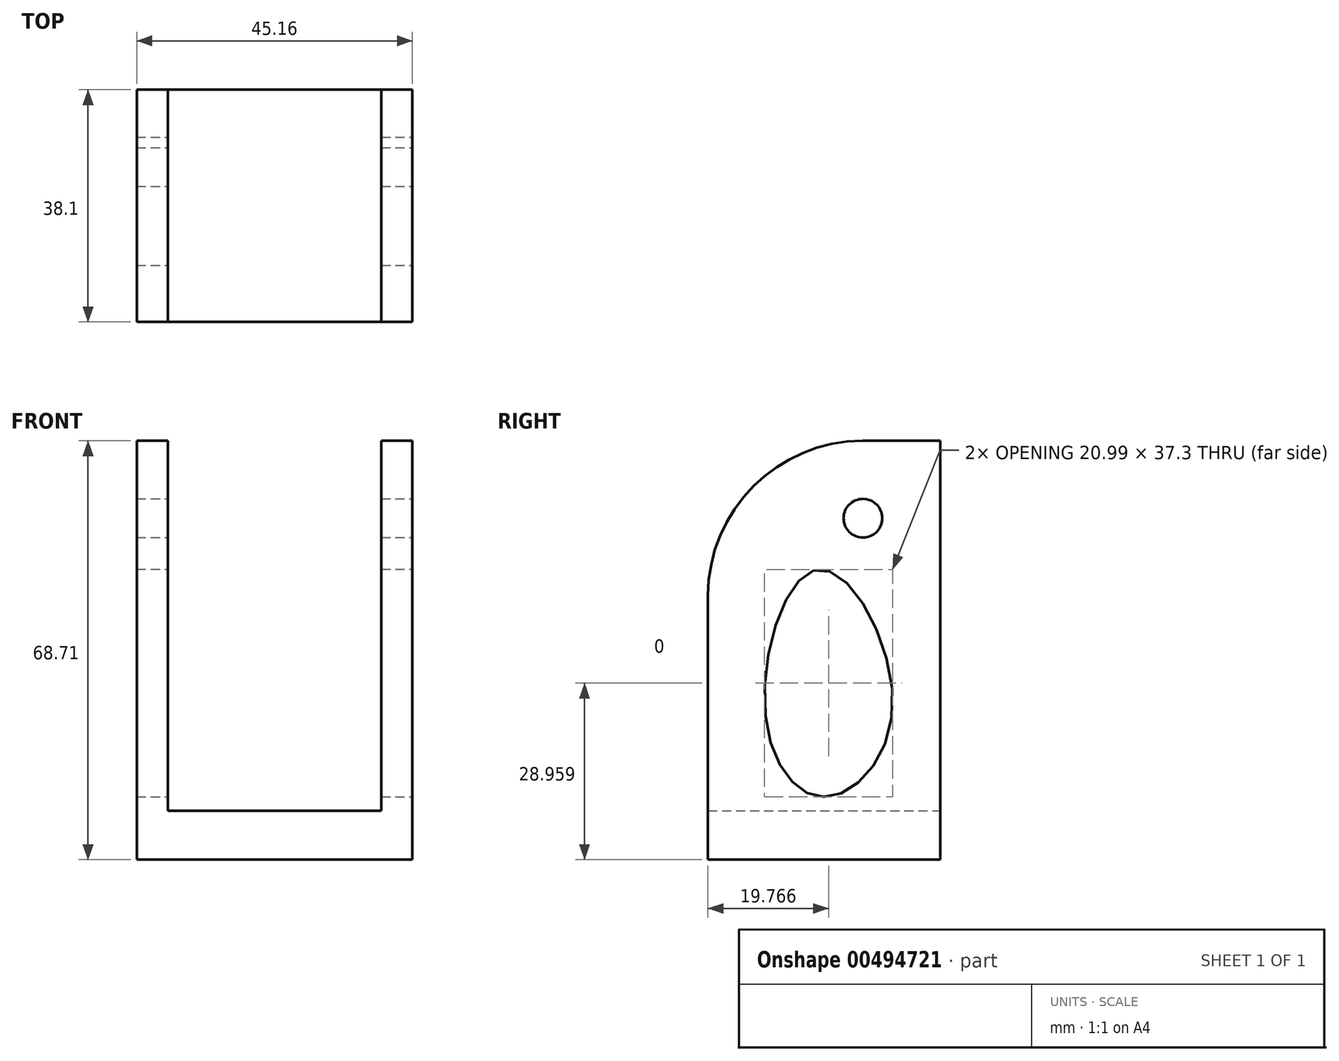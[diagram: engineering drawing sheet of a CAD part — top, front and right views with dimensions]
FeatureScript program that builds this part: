
annotation { "Feature Type Name" : "Feature", "Feature Type Description" : "" }
export const myFeature = defineFeature(function(context is Context, id is Id, definition is map)
    precondition{}
    {
        {
            var Q0;
            Q0=qCreatedBy(makeId("Front.planeOp"),FACE);
            var sketch = newSketch(context, id + "F0", { "sketchPlane" : qUnion([Q0])});
            skLineSegment(sketch, "E0.bottom", {"start": v(0, 0) * mm, "end": v(-45.16, 0) * mm});
            skLineSegment(sketch, "E0.top", {"start": v(0, 8.02) * mm, "end": v(-45.16, 8.02) * mm});
            skLineSegment(sketch, "E0.left", {"start": v(0, 0) * mm, "end": v(0, 8.02) * mm});
            skLineSegment(sketch, "E0.right", {"start": v(-45.16, 0) * mm, "end": v(-45.16, 8.02) * mm});
            skLineSegment(sketch, "E1.bottom", {"start": v(-45.16, 8.02) * mm, "end": v(-40.08, 8.02) * mm});
            skLineSegment(sketch, "E1.top", {"start": v(-45.16, 68.71) * mm, "end": v(-40.08, 68.71) * mm});
            skLineSegment(sketch, "E1.left", {"start": v(-45.16, 8.02) * mm, "end": v(-45.16, 68.71) * mm});
            skLineSegment(sketch, "E1.right", {"start": v(-40.08, 8.02) * mm, "end": v(-40.08, 68.71) * mm});
            skLineSegment(sketch, "E2.bottom", {"start": v(0, 8.02) * mm, "end": v(-5.08, 8.02) * mm});
            skLineSegment(sketch, "E2.top", {"start": v(0, 68.71) * mm, "end": v(-5.08, 68.71) * mm});
            skLineSegment(sketch, "E2.left", {"start": v(0, 8.02) * mm, "end": v(0, 68.71) * mm});
            skLineSegment(sketch, "E2.right", {"start": v(-5.08, 8.02) * mm, "end": v(-5.08, 68.71) * mm});
            skSolve(sketch);
        }
        {
            var Q0;
            Q0=qSketchRegion(id+"F0",true);
            var Q1;
            Q1=qSketchRegion(id+"F2",true);
            extrude(context, id + "F1", {"entities" : qUnion([Q0, Q1]), "depth" : 38.1 * mm});
        }
        {
            var Q0;
            Q0=qCreatedBy(makeId("Right.planeOp"),FACE);
            var sketch = newSketch(context, id + "F2", { "sketchPlane" : qUnion([Q0])});
            skPoint(sketch, "E3", {"position": v(-12.7, 56.01) * mm});
            skFitSpline(sketch, "E4", {"points": [v(-19.14, 10.3) * mm, v(-28.72, 24.05) * mm, v(-19.88, 47.61) * mm, v(-7.85, 24.79) * mm, v(-19.14, 10.3) * mm]});
            skPoint(sketch, "E5", {"position": v(-31.8, 8.37) * mm});
            skSolve(sketch);
        }
        {
            var Q0;
            Q0=sQuery(id+"F2.wireOp",VERTEX,"E3");
            var Q1;
            Q1=makeQuery(id+"F1.opExtrude","SWEPT_BODY",BODY,{"disambiguationData":[OSD([sQuery(id+"F0.wireOp",EDGE,"E0.bottom"),sQuery(id+"F0.wireOp",EDGE,"E0.top"),sQuery(id+"F0.wireOp",EDGE,"E0.left"),sQuery(id+"F0.wireOp",EDGE,"E0.right"),sQuery(id+"F0.wireOp",EDGE,"E1.top"),sQuery(id+"F0.wireOp",EDGE,"E1.left"),sQuery(id+"F0.wireOp",EDGE,"E1.right"),sQuery(id+"F0.wireOp",EDGE,"E2.top"),sQuery(id+"F0.wireOp",EDGE,"E2.left"),sQuery(id+"F0.wireOp",EDGE,"E2.right")])]});
            hole(context, id + "F3", {"style" : HoleStyle.SIMPLE, "endStyle" : HoleEndStyle.THROUGH, "holeDiameter" : 6.35 * mm, "isTappedThrough" : true, "tappedDepth" : 12.7 * mm, "tapClearance" : 3, "locations" : qUnion([Q0]), "scope" : qUnion([Q1])});
        }
        {
            var Q0;
            Q0=qSketchRegion(id+"F2",true);
            extrude(context, id + "F4", {"entities" : qUnion([Q0]), "operationType" : NewBodyOperationType.REMOVE, "endBound" : BoundingType.THROUGH_ALL, "oppositeDirection" : true, "depth" : 25.4 * mm});
        }
        {
            var Q0;
            Q0=makeQuery(id+"F1.opExtrude","CAP_EDGE",EDGE,{"disambiguationData":[OSD([sQuery(id+"F0.wireOp",EDGE,"E2.top")])],"isStart":false});
            var Q1;
            Q1=makeQuery(id+"F1.opExtrude","CAP_EDGE",EDGE,{"disambiguationData":[OSD([sQuery(id+"F0.wireOp",EDGE,"E1.top")])],"isStart":false});
            fillet(context, id + "F5", {"entities" : qUnion([Q0, Q1]), "radius" : 25.4 * mm, "tangentPropagation" : true, "allowEdgeOverflow" : false});
        }
    });
